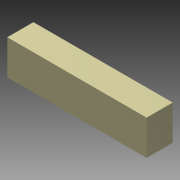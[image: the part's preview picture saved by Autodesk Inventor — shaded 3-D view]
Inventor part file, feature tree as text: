
AUTODESK INVENTOR PART (.ipt)
format: ipt  version: 2015 (Build 190159000, 159)  size: 73,216 bytes
history: native  units: mm
features: other x1, extrude x1, sketch x1
ambient origin geometry x8: Origin, YZ Plane, XZ Plane, XY Plane, X Axis, Y Axis, Z Axis, Center Point
bodies: Body1 (feature_tree)
feature tree (3):
  other  "ソリッド1"
  extrude  "押し出し1"  Depth=80.0mm
  sketch  "スケッチ1"
